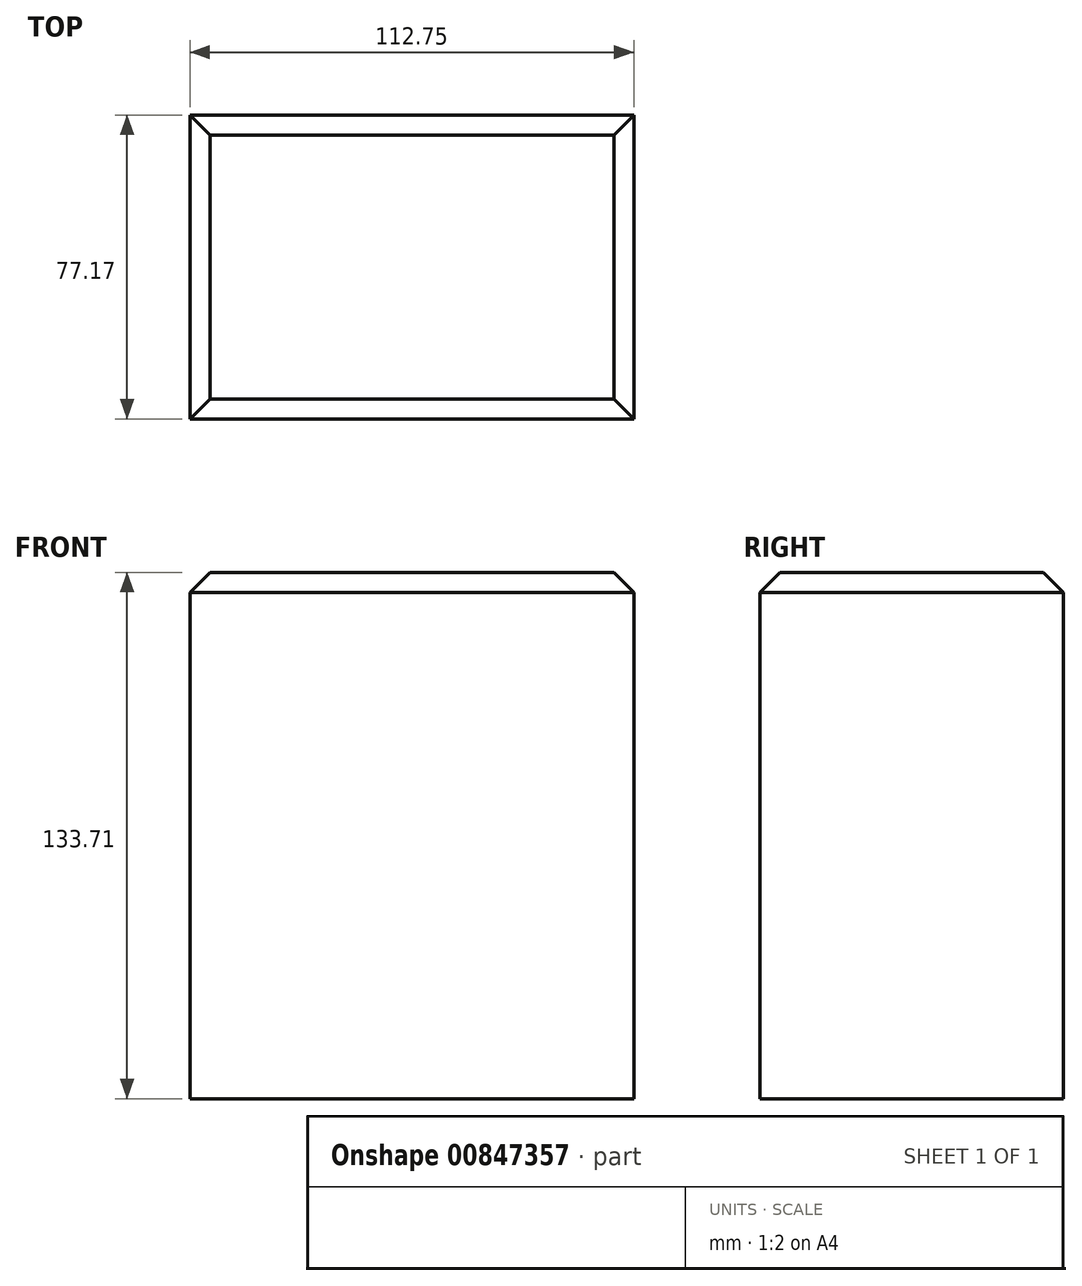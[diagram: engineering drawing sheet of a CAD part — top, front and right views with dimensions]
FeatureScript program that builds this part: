
annotation { "Feature Type Name" : "Feature", "Feature Type Description" : "" }
export const myFeature = defineFeature(function(context is Context, id is Id, definition is map)
    precondition{}
    {
        {
            var Q0;
            Q0=qCreatedBy(makeId("Top.planeOp"),FACE);
            var sketch = newSketch(context, id + "F0", { "sketchPlane" : qUnion([Q0])});
            skLineSegment(sketch, "E0.bottom", {"start": v(-80.3, 0) * mm, "end": v(32.44, 0) * mm});
            skLineSegment(sketch, "E0.top", {"start": v(-80.3, -77.17) * mm, "end": v(32.44, -77.17) * mm});
            skLineSegment(sketch, "E0.left", {"start": v(-80.3, 0) * mm, "end": v(-80.3, -77.17) * mm});
            skLineSegment(sketch, "E0.right", {"start": v(32.44, 0) * mm, "end": v(32.44, -77.17) * mm});
            skSolve(sketch);
        }
        {
            var Q0;
            Q0=makeQuery(id+"F0.imprint","IMPRINT",FACE,{"disambiguationData":[TD([[makeQuery(id+"F0.imprint","IMPRINT",EDGE,{"derivedFrom":sQuery(id+"F0.wireOp",EDGE,"E0.bottom")}),-1.0]])]});
            extrude(context, id + "F1", {"entities" : qUnion([Q0]), "depth" : 133.7 * mm, "offsetDistance" : 25.4 * mm});
        }
        {
            var Q0;
            Q0=makeQuery(id+"F1.opExtrude","CAP_FACE",FACE,{"disambiguationData":[OSD([sQuery(id+"F0.wireOp",EDGE,"E0.bottom"),sQuery(id+"F0.wireOp",EDGE,"E0.top"),sQuery(id+"F0.wireOp",EDGE,"E0.left"),sQuery(id+"F0.wireOp",EDGE,"E0.right")])],"isStart":false});
            chamfer(context, id + "F2", {"entities" : qUnion([Q0]), "width" : 5.08 * mm, "tangentPropagation" : true});
        }
    });
